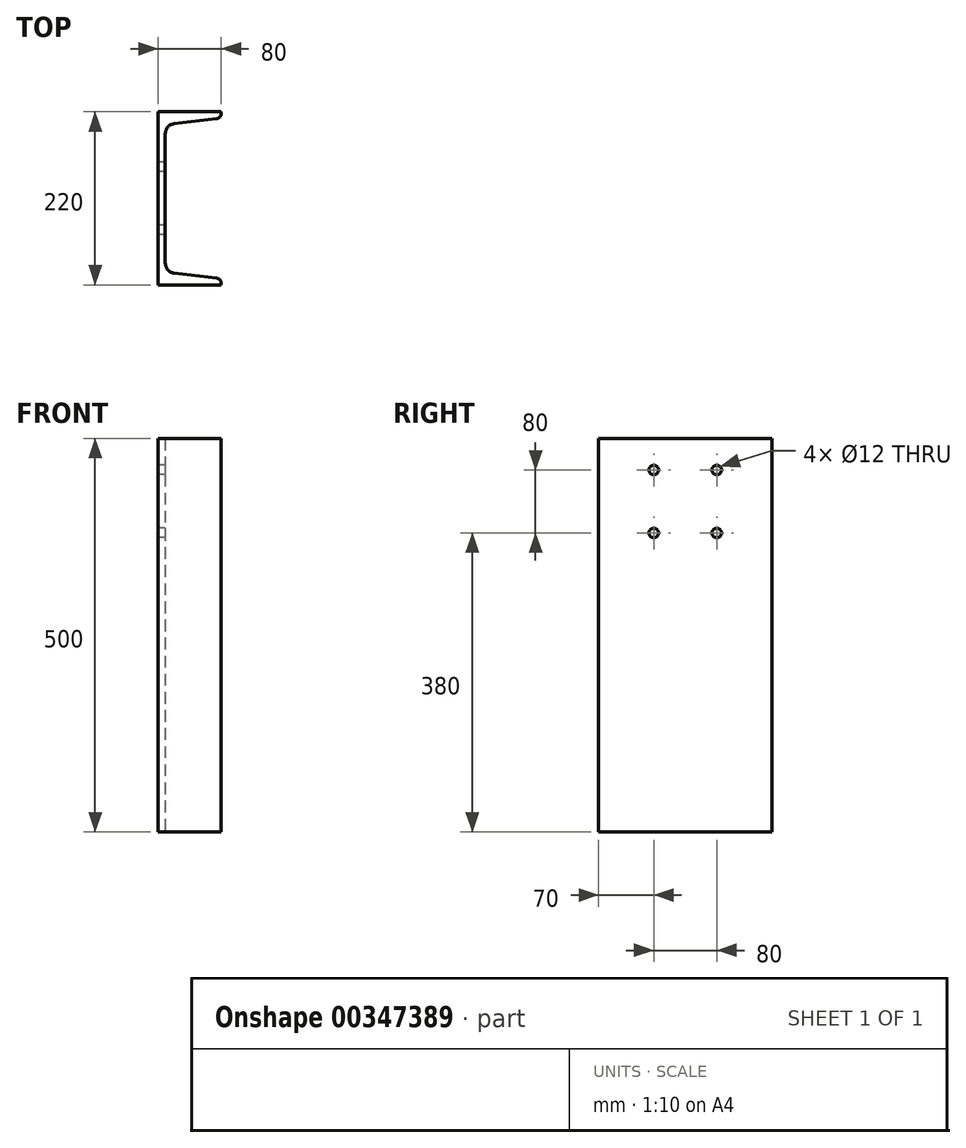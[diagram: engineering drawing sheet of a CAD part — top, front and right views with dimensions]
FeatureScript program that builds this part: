
annotation { "Feature Type Name" : "Feature", "Feature Type Description" : "" }
export const myFeature = defineFeature(function(context is Context, id is Id, definition is map)
    precondition{}
    {
        {
            var Q0;
            Q0=qCreatedBy(makeId("Top.planeOp"),FACE);
            var sketch = newSketch(context, id + "F0", { "sketchPlane" : qUnion([Q0])});
            skLineSegment(sketch, "E0", {"start": v(0, 0) * mm, "end": v(0, 110) * mm});
            skLineSegment(sketch, "E1", {"start": v(0, 0) * mm, "end": v(80, 0) * mm});
            skLineSegment(sketch, "E2.0", {"start": v(9, 27.6) * mm, "end": v(9, 110) * mm});
            skLineSegment(sketch, "E3", {"start": v(80, 0) * mm, "end": v(80, 2.23) * mm});
            skLineSegment(sketch, "E4", {"start": v(74.27, 8.69) * mm, "end": v(20.01, 15.2) * mm});
            skPoint(sketch, "E5.orphan", {"position": v(42.5, 12.5) * mm});
            skArc(sketch, "E6.filletArc", {"start": v(9, 27.6) * mm, "mid": v(12.15, 19.31) * mm, "end": v(20.01, 15.2) * mm});
            skPoint(sketch, "E7.visualSharp", {"position": v(80, 8) * mm});
            skArc(sketch, "E7.filletArc", {"start": v(80, 2.23) * mm, "mid": v(78.36, 6.55) * mm, "end": v(74.27, 8.69) * mm});
            skLineSegment(sketch, "E8", {"start": v(42.5, 12.5) * mm, "end": v(42.5, 0) * mm, "construction": true});
            skLineSegment(sketch, "E9", {"start": v(0, 110) * mm, "end": v(9, 110) * mm, "construction": true});
            skLineSegment(sketch, "E10.MirrorCS", {"start": v(42.5, 207.5) * mm, "end": v(42.5, 220) * mm, "construction": true});
            skLineSegment(sketch, "E11.MirrorCS", {"start": v(80, 220) * mm, "end": v(80, 217.77) * mm});
            skArc(sketch, "E12.MirrorCS", {"start": v(80, 217.77) * mm, "mid": v(78.36, 213.45) * mm, "end": v(74.27, 211.31) * mm});
            skPoint(sketch, "E13.MirrorP", {"position": v(42.5, 207.5) * mm});
            skLineSegment(sketch, "E14.MirrorCS", {"start": v(0, 220) * mm, "end": v(0, 110) * mm});
            skLineSegment(sketch, "E15.MirrorCS", {"start": v(0, 220) * mm, "end": v(80, 220) * mm});
            skLineSegment(sketch, "E16.MirrorCS", {"start": v(9, 192.4) * mm, "end": v(9, 110) * mm});
            skPoint(sketch, "E17.MirrorP", {"position": v(80, 212) * mm});
            skLineSegment(sketch, "E18.MirrorCS", {"start": v(74.27, 211.31) * mm, "end": v(20.01, 204.8) * mm});
            skArc(sketch, "E19.MirrorCS", {"start": v(9, 192.4) * mm, "mid": v(12.15, 200.69) * mm, "end": v(20.01, 204.8) * mm});
            skSolve(sketch);
        }
        {
            var Q0;
            Q0=makeQuery(id+"F0.imprint","IMPRINT",FACE,{"disambiguationData":[TD([[makeQuery(id+"F0.imprint","IMPRINT",EDGE,{"derivedFrom":sQuery(id+"F0.wireOp",EDGE,"E0")}),-1.0]])]});
            extrude(context, id + "F1", {"entities" : qUnion([Q0]), "endBound" : BoundingType.SYMMETRIC, "depth" : 500 * mm});
        }
        {
            var Q0;
            Q0=makeQuery(id+"F1.opExtrude","SWEPT_FACE",FACE,{"disambiguationData":[OSD([sQuery(id+"F0.wireOp",EDGE,"E0"),sQuery(id+"F0.wireOp",EDGE,"5ec7c80c-e505-447a-9aef-a8a587834d0f8.MirrorCS")])]});
            var sketch = newSketch(context, id + "F2", { "sketchPlane" : qUnion([Q0])});
            skLineSegment(sketch, "E20", {"start": v(18.26, 210) * mm, "end": v(-233.77, 210) * mm, "construction": true});
            skLineSegment(sketch, "E21", {"start": v(-70, -96.93) * mm, "end": v(-70, 240.61) * mm, "construction": true});
            skLineSegment(sketch, "E22", {"start": v(-110, 250) * mm, "end": v(-110, -139.95) * mm, "construction": true});
            skPoint(sketch, "E22.endSnap0", {"position": v(-110, 250) * mm});
            skLineSegment(sketch, "E23", {"start": v(-150, 228.97) * mm, "end": v(-150, -127.8) * mm, "construction": true});
            skLineSegment(sketch, "E24.0", {"start": v(18.26, 130) * mm, "end": v(-233.77, 130) * mm, "construction": true});
            skCircle(sketch, "E25", {"center": v(-70, 130) * mm, "radius": 6 * mm});
            skCircle(sketch, "E26", {"center": v(-150, 130) * mm, "radius": 6 * mm});
            skCircle(sketch, "E27", {"center": v(-70, 210) * mm, "radius": 6 * mm});
            skCircle(sketch, "E28", {"center": v(-150, 210) * mm, "radius": 6 * mm});
            skSolve(sketch);
        }
        {
            var Q0;
            Q0=makeQuery(id+"F2.imprint","IMPRINT",FACE,{"disambiguationData":[TD([[makeQuery(id+"F2.imprint","IMPRINT",EDGE,{"derivedFrom":sQuery(id+"F2.wireOp",EDGE,"E27")}),1.0]])]});
            var Q1;
            Q1=makeQuery(id+"F2.imprint","IMPRINT",FACE,{"disambiguationData":[TD([[makeQuery(id+"F2.imprint","IMPRINT",EDGE,{"derivedFrom":sQuery(id+"F2.wireOp",EDGE,"E28")}),1.0]])]});
            var Q2;
            Q2=makeQuery(id+"F2.imprint","IMPRINT",FACE,{"disambiguationData":[TD([[makeQuery(id+"F2.imprint","IMPRINT",EDGE,{"derivedFrom":sQuery(id+"F2.wireOp",EDGE,"E25")}),1.0]])]});
            var Q3;
            Q3=makeQuery(id+"F2.imprint","IMPRINT",FACE,{"disambiguationData":[TD([[makeQuery(id+"F2.imprint","IMPRINT",EDGE,{"derivedFrom":sQuery(id+"F2.wireOp",EDGE,"E26")}),1.0]])]});
            extrude(context, id + "F3", {"entities" : qUnion([Q0, Q1, Q2, Q3]), "operationType" : NewBodyOperationType.REMOVE, "endBound" : BoundingType.THROUGH_ALL, "oppositeDirection" : true, "depth" : 25 * mm});
        }
    });
